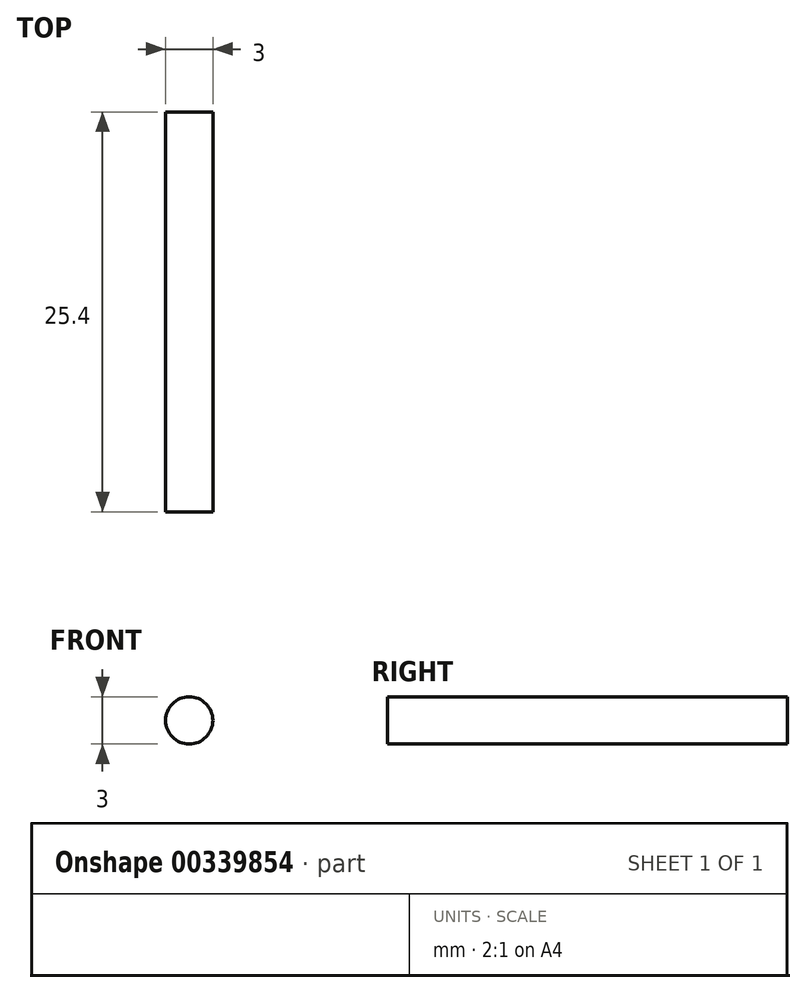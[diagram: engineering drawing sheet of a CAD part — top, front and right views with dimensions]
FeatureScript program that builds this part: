
annotation { "Feature Type Name" : "Feature", "Feature Type Description" : "" }
export const myFeature = defineFeature(function(context is Context, id is Id, definition is map)
    precondition{}
    {
        {
            var Q0;
            Q0=qCreatedBy(makeId("Front.planeOp"),FACE);
            var sketch = newSketch(context, id + "F0", { "sketchPlane" : qUnion([Q0])});
            skCircle(sketch, "E0", {"center": v(-18.4, 22.5) * mm, "radius": 1.5 * mm});
            skSolve(sketch);
        }
        {
            var Q0;
            Q0=makeQuery(id+"F0.imprint","IMPRINT",FACE,{"disambiguationData":[TD([[makeQuery(id+"F0.imprint","IMPRINT",EDGE,{"derivedFrom":sQuery(id+"F0.wireOp",EDGE,"E0")}),1.0]])]});
            extrude(context, id + "F1", {"entities" : qUnion([Q0]), "depth" : 25.4 * mm});
        }
    });
